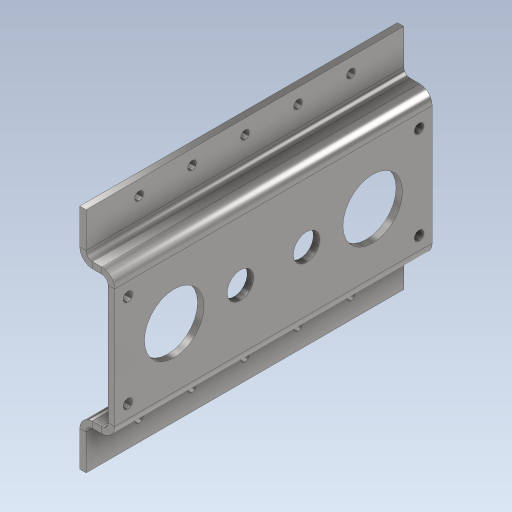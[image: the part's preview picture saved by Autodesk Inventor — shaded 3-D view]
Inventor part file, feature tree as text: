
AUTODESK INVENTOR PART (.ipt)
format: ipt  version: 2023 (Build 270158000, 158)  size: 258,560 bytes
history: native  units: in
note: dims shown in document units (in); Inventor stores cm internally (conversion verified against a paired STEP export)
features: sheet_metal_op x7, sketch x5, other x3, hole x2, projected_geometry x1
ambient origin geometry x8: Origin, YZ Plane, XZ Plane, XY Plane, X Axis, Y Axis, Z Axis, Center Point
bodies: Body1 (feature_tree)
feature tree (18):
  sheet_metal_op  "Face2"
  sheet_metal_op  "Flange1"
  sheet_metal_op  "Flange2"
  hole  "Hole2"  [1 undecoded]
  hole  "Hole1"  [1 undecoded]
  sketch  "Sketch1"  dims[d0=2.25in d1=6.0in]
  other  "Plate2"
  sketch  "Sketch2"  dims[d2=1.25in d3=1.25in]
  other  "Plate3"
  sheet_metal_op  "Bend1"
  sheet_metal_op  "Corner1"
  sketch  "Sketch3"  dims[d4=1.25in]
  projected_geometry  "Projected Loop1"
  sketch  "Sketch4"  dims[d6=1.125in]
  other  "Plate4"
  sheet_metal_op  "Bend2"
  sheet_metal_op  "Corner2"
  sketch  "Sketch5"  dims[d7=0.5in d8=1.125in d10=0.12in d11=0.177in d12=5.5in d13=1.75in d14=0.5in d15=6.0in d16=0.5in d17=6.0in d18=0.12in d19=0.06in d20=0.24in d21=0.12in d22=0.6583in d23=90.0deg d24=0.12in d25=0.48in d26=0.12in d27=0.12in d28=1.0in d29=1.9685in d31=1.0in d32=0.3937in d34=1.0in d36=0.1628in d37=5.0in d38=0.375in d39=0.25in d40=0.5635in d41=0.12in d42=0.8108in d43=0.12in d44=0.06in d45=0.24in d46=0.12in d47=0.7874in d48=90.0deg d49=0.12in d50=0.48in d51=0.12in d52=0.12in d53=1.0in d54=0.3937in d55=1.9685in d57=1.0in d58=0.3937in d60=1.0in d62=0.1628in d63=0.394in d64=0.375in d65=0.25in d66=0.5635in d67=1.0in d68=0.8108in d69=0.3937in d71=1.0in d72=0.7874in d74=3.6374in]
note: 2 required parameter values undecoded (feature->parameter linkage not recoverable at this tier; creation-order binding heuristic only, values carry confidence <= 0.55)
